# Revit family: PH_2815-2865-2606_OS265
name_source: partatom
category: Finestre
units: mm (PartAtom-declared; Revit-internal decimal feet)

## family parameters
Condiviso = No
Host = Muro
Numero OmniClass = 23.30.20.00
Punto di calcolo locali = Sì
Sempre verticale = Sì
Taglio con vuoti quando caricato = No
Titolo OmniClass = Windows

## types (4) — shared parameters
Altezza di default del davanzale = 800 mm
Chiusura muro = Per host
Costruzione analitica = <Nessuno>
Descrizione = finestra a bilico orizzontale
H_Max = 1300 mm
H_Min = 600 mm
L_Max = 2000 mm  [stored 6.56168 ft]
L_Min = 600 mm
Modello = OS2 75
Nota tecnica = https://s3-eu-central-1.amazonaws.com
Produttore = Secco Sistemi Spa
URL = https://www.seccosistemi.com

## per-type parameters (varying)
| type | Altezza | Altezza_1A | Altezza_2A | Altezza_ante | H1 | H_Telaio_E | H_Telaio_I | H_vetro | L1 | L_Telaio_E | L_Telaio_I | L_vetro | Larghezza | Larghezza_ante | MATERIALE | WARNING |
| Ottone | 1000 mm  [stored 3.28084 ft] | 485 mm | 485 mm | 970 mm  [stored 3.18241 ft] | 1000 mm  [stored 3.28084 ft] | 500 mm  [stored 1.64042 ft] | 500 mm  [stored 1.64042 ft] | 894 mm  [stored 2.93307 ft] | 1800 mm | 900 mm | 900 mm | 1694 mm | 1800 mm | 1770 mm | Ottone | No |
| Acciaio zincato | 1500 mm | 635 mm | 635 mm | 1270 mm | 1300 mm | 650 mm  [stored 2.13255 ft] | 650 mm  [stored 2.13255 ft] | 1194 mm | 1000 mm  [stored 3.28084 ft] | 500 mm  [stored 1.64042 ft] | 500 mm  [stored 1.64042 ft] | 894 mm  [stored 2.93307 ft] | 1000 mm  [stored 3.28084 ft] | 970 mm  [stored 3.18241 ft] | Acciaio | Sì |
| Acciaio inox | 1500 mm | 635 mm | 635 mm | 1270 mm | 1300 mm | 650 mm  [stored 2.13255 ft] | 650 mm  [stored 2.13255 ft] | 1194 mm | 1000 mm  [stored 3.28084 ft] | 500 mm  [stored 1.64042 ft] | 500 mm  [stored 1.64042 ft] | 894 mm  [stored 2.93307 ft] | 1000 mm  [stored 3.28084 ft] | 970 mm  [stored 3.18241 ft] | Acciaio inox, spazzolato | Sì |
| Acciaio Corten | 1500 mm | 635 mm | 635 mm | 1270 mm | 1300 mm | 650 mm  [stored 2.13255 ft] | 650 mm  [stored 2.13255 ft] | 1194 mm | 1000 mm  [stored 3.28084 ft] | 500 mm  [stored 1.64042 ft] | 500 mm  [stored 1.64042 ft] | 894 mm  [stored 2.93307 ft] | 1000 mm  [stored 3.28084 ft] | 970 mm  [stored 3.18241 ft] | Acciaio corten | Sì |

note: [stored X ft] marks values corroborated as IEEE doubles in the binary element streams (Revit-internal decimal feet)
